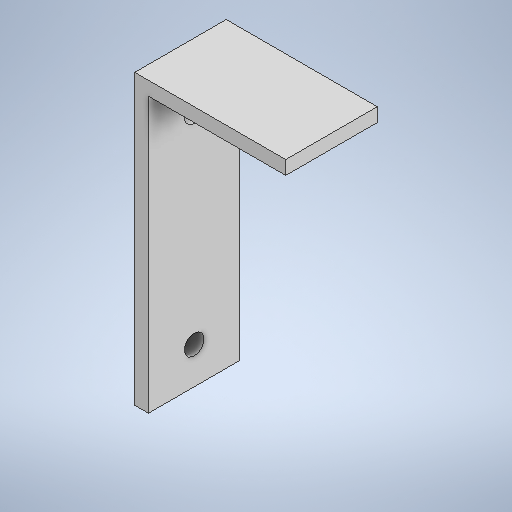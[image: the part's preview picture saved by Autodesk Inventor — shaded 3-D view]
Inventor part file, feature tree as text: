
AUTODESK INVENTOR PART (.ipt)
format: ipt  version: 2025.2 (Build 292293000, 293)  size: 238,592 bytes
history: native  units: mm
features: extrude x2, sketch x2
ambient origin geometry x8: Origin, YZ Plane, XZ Plane, XY Plane, X Axis, Y Axis, Z Axis, Center Point
bodies: Solid1 (feature_tree)
feature tree (4):
  extrude  "Extrusion1"  Depth=60.0mm
  extrude  "Extrusion2"  Depth=3.0mm
  sketch  "Sketch1"  dims[d0=30.0mm d1=60.0mm]
  sketch  "Sketch2"  dims[d2=3.0mm d3=3.0mm d4=20.0mm d5=0.0mm d6=8.0mm d7=8.0mm d8=4.3mm d9=4.3mm d10=0.0mm d11=0.0mm]
